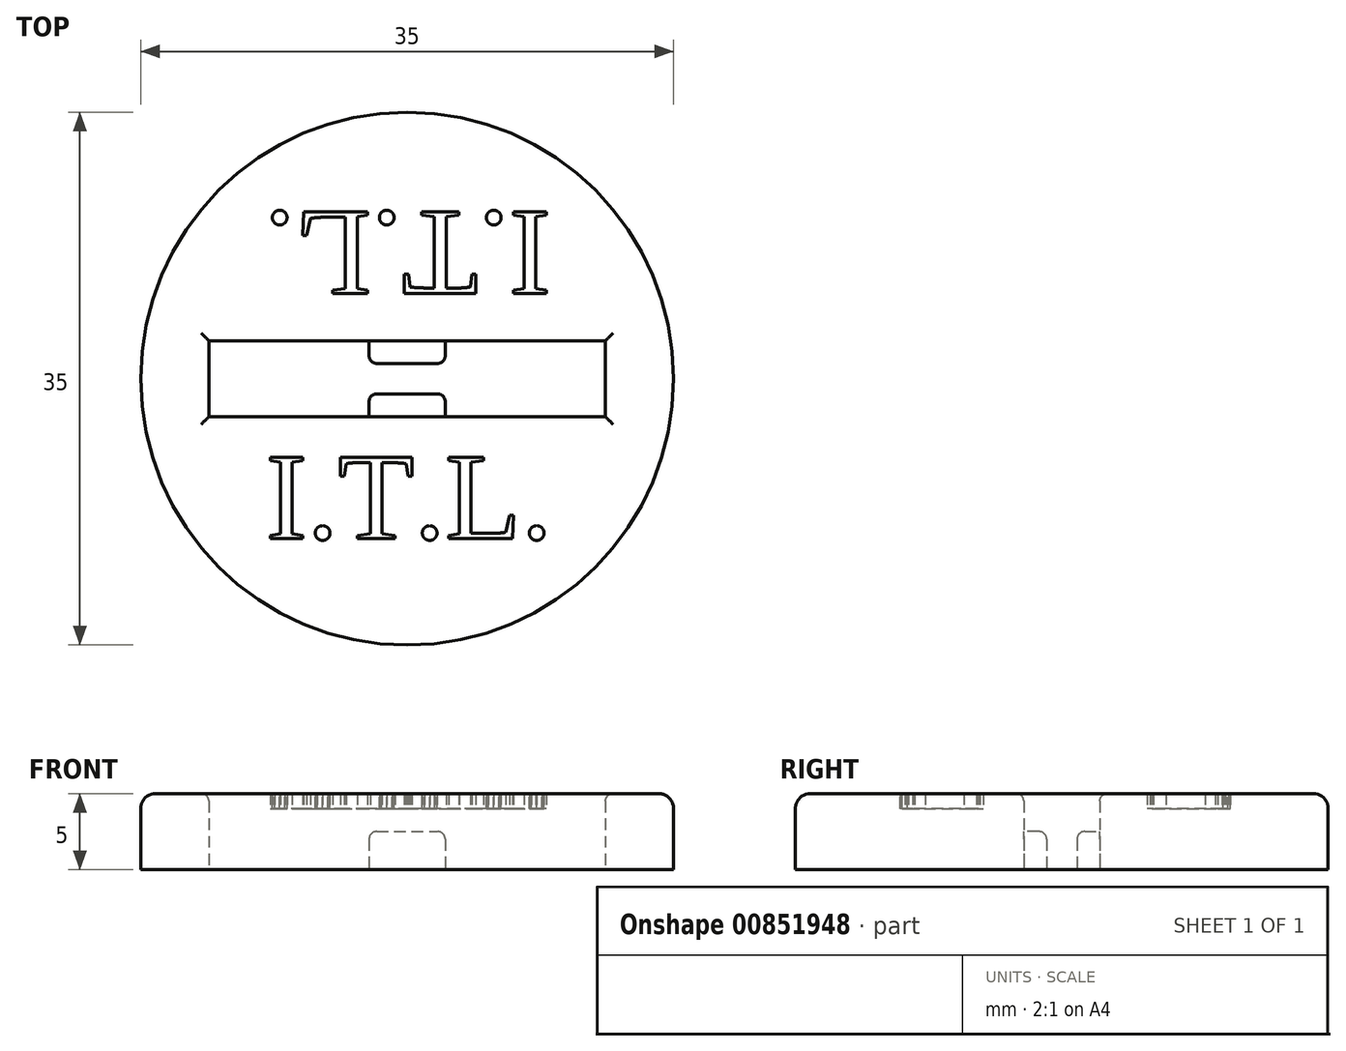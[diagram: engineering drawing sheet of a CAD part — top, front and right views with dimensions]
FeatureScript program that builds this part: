
annotation { "Feature Type Name" : "Feature", "Feature Type Description" : "" }
export const myFeature = defineFeature(function(context is Context, id is Id, definition is map)
    precondition{}
    {
        {
            var Q0;
            Q0=qCreatedBy(makeId("Top.planeOp"),FACE);
            var sketch = newSketch(context, id + "F0", { "sketchPlane" : qUnion([Q0])});
            skPoint(sketch, "E0.middle", {"position": v(0, 0) * mm});
            skLineSegment(sketch, "E1", {"start": v(2.5, -1) * mm, "end": v(-2.5, -1) * mm});
            skLineSegment(sketch, "E2", {"start": v(-2.5, 1) * mm, "end": v(2.5, 1) * mm});
            skCircle(sketch, "E3", {"center": v(0, 0) * mm, "radius": 17.5 * mm});
            skText(sketch, "E4", { "text": "I.T.L.", "fontName": "Tinos-Regular.ttf"});
            skText(sketch, "E5", { "text": "I.T.L.", "fontName": "Tinos-Regular.ttf"});
            skLineSegment(sketch, "E6", {"start": v(2.5, -1) * mm, "end": v(2.5, -2.5) * mm});
            skLineSegment(sketch, "E7", {"start": v(-2.5, -1) * mm, "end": v(-2.5, -2.5) * mm});
            skLineSegment(sketch, "E8", {"start": v(-2.5, 1) * mm, "end": v(-2.5, 2.5) * mm});
            skLineSegment(sketch, "E9", {"start": v(2.5, 1) * mm, "end": v(2.5, 2.5) * mm});
            skLineSegment(sketch, "E10", {"start": v(13.03, -2.5) * mm, "end": v(13.03, 2.5) * mm});
            skLineSegment(sketch, "E11", {"start": v(-13.03, 2.5) * mm, "end": v(-13.03, -2.5) * mm});
            skLineSegment(sketch, "E12", {"start": v(13.03, -2.5) * mm, "end": v(-13.03, -2.5) * mm});
            skLineSegment(sketch, "E13", {"start": v(-13.03, 2.5) * mm, "end": v(13.03, 2.5) * mm});
            const initialGuessF0  = {"E4": [-0.00929, -0.01051, 1, 0, 0.00588], "E5": [0.00943, 0.01095, -1, 0, 0.00588]};
            skSetInitialGuess(sketch, initialGuessF0);
            skSolve(sketch);
        }
        {
            var Q0;
            Q0 = qSketchRegion(id + "F0", true);
            extrude(context, id + "F1", {"entities" : qUnion([Q0]), "depth" : 5 * mm, "offsetDistance" : 25 * mm});
        }
        {
            var Q0;
            Q0=makeQuery(id+"F1.opExtrude","CAP_EDGE",EDGE,{"disambiguationData":[OSD([sQuery(id+"F0.wireOp",EDGE,"99ddf1c2-c051-48f3-a438-be00599b5eb5.bottom")])],"isStart":false});
            var Q1;
            Q1=makeQuery(id+"F1.opExtrude","CAP_EDGE",EDGE,{"disambiguationData":[OSD([sQuery(id+"F0.wireOp",EDGE,"99ddf1c2-c051-48f3-a438-be00599b5eb5.left")])],"isStart":false});
            var Q2;
            Q2=makeQuery(id+"F1.opExtrude","CAP_EDGE",EDGE,{"disambiguationData":[OSD([sQuery(id+"F0.wireOp",EDGE,"99ddf1c2-c051-48f3-a438-be00599b5eb5.top")])],"isStart":false});
            var Q3;
            Q3=makeQuery(id+"F1.opExtrude","CAP_EDGE",EDGE,{"disambiguationData":[OSD([sQuery(id+"F0.wireOp",EDGE,"99ddf1c2-c051-48f3-a438-be00599b5eb5.right")])],"isStart":false});
            var Q4;
            Q4=makeQuery(id+"F1.opExtrude","CAP_EDGE",EDGE,{"disambiguationData":[OSD([sQuery(id+"F0.wireOp",EDGE,"E13")])],"isStart":false});
            var Q5;
            Q5=makeQuery(id+"F1.opExtrude","CAP_EDGE",EDGE,{"disambiguationData":[OSD([sQuery(id+"F0.wireOp",EDGE,"E10")])],"isStart":false});
            var Q6;
            Q6=makeQuery(id+"F1.opExtrude","CAP_EDGE",EDGE,{"disambiguationData":[OSD([sQuery(id+"F0.wireOp",EDGE,"E12")])],"isStart":false});
            var Q7;
            Q7=makeQuery(id+"F1.opExtrude","CAP_EDGE",EDGE,{"disambiguationData":[OSD([sQuery(id+"F0.wireOp",EDGE,"E11")])],"isStart":false});
            fillet(context, id + "F2", {"entities" : qUnion([Q0, Q1, Q2, Q3, Q4, Q5, Q6, Q7]), "radius" : .5 * mm, "tangentPropagation" : true, "defaultsChanged" : false, "vertexSettings" : [], "allowEdgeOverflow" : false});
        }
        {
            var Q0;
            Q0=makeQuery(id+"F1.opExtrude","CAP_EDGE",EDGE,{"disambiguationData":[OSD([sQuery(id+"F0.wireOp",EDGE,"E3")])],"isStart":false});
            fillet(context, id + "F3", {"entities" : qUnion([Q0]), "radius" : 1 * mm, "tangentPropagation" : true, "allowEdgeOverflow" : false});
        }
        {
            var Q0;
            Q0=makeQuery(id+"F0.imprint","IMPRINT",FACE,{"disambiguationData":[TD([[makeQuery(id+"F0.imprint","IMPRINT",EDGE,{"derivedFrom":sQuery(id+"F0.wireOp",EDGE,"E2")}),1.0]])]});
            var Q1;
            Q1=makeQuery(id+"F0.imprint","IMPRINT",FACE,{"disambiguationData":[TD([[makeQuery(id+"F0.imprint","IMPRINT",EDGE,{"derivedFrom":sQuery(id+"F0.wireOp",EDGE,"E1")}),1.0]])]});
            extrude(context, id + "F4", {"entities" : qUnion([Q0, Q1]), "operationType" : NewBodyOperationType.ADD, "depth" : 2.5 * mm, "offsetDistance" : 25 * mm});
        }
        {
            var Q0;
            Q0=makeQuery(id+"F0.imprint","IMPRINT",FACE,{"disambiguationData":[TD([[makeQuery(id+"F0.imprint","IMPRINT",EDGE,{"derivedFrom":sQuery(id+"F0.wireOp",EDGE,"E4.sketch_text.stroke-47")}),-1.0]])]});
            var Q1;
            Q1=makeQuery(id+"F0.imprint","IMPRINT",FACE,{"disambiguationData":[TD([[makeQuery(id+"F0.imprint","IMPRINT",EDGE,{"derivedFrom":sQuery(id+"F0.wireOp",EDGE,"E4.sketch_text.stroke-62")}),-1.0]])]});
            var Q2;
            Q2=makeQuery(id+"F0.imprint","IMPRINT",FACE,{"disambiguationData":[TD([[makeQuery(id+"F0.imprint","IMPRINT",EDGE,{"derivedFrom":sQuery(id+"F0.wireOp",EDGE,"E4.sketch_text.stroke-39")}),-1.0]])]});
            var Q3;
            Q3=makeQuery(id+"F0.imprint","IMPRINT",FACE,{"disambiguationData":[TD([[makeQuery(id+"F0.imprint","IMPRINT",EDGE,{"derivedFrom":sQuery(id+"F0.wireOp",EDGE,"E4.sketch_text.stroke-20")}),-1.0]])]});
            var Q4;
            Q4=makeQuery(id+"F0.imprint","IMPRINT",FACE,{"disambiguationData":[TD([[makeQuery(id+"F0.imprint","IMPRINT",EDGE,{"derivedFrom":sQuery(id+"F0.wireOp",EDGE,"E4.sketch_text.stroke-12")}),-1.0]])]});
            var Q5;
            Q5=makeQuery(id+"F0.imprint","IMPRINT",FACE,{"disambiguationData":[TD([[makeQuery(id+"F0.imprint","IMPRINT",EDGE,{"derivedFrom":sQuery(id+"F0.wireOp",EDGE,"E4.sketch_text.stroke-0")}),-1.0]])]});
            extrude(context, id + "F5", {"entities" : qUnion([Q0, Q1, Q2, Q3, Q4, Q5]), "operationType" : NewBodyOperationType.ADD, "depth" : 4 * mm, "offsetDistance" : 25 * mm});
        }
        {
            var Q0;
            Q0=makeQuery(id+"F0.imprint","IMPRINT",FACE,{"disambiguationData":[TD([[makeQuery(id+"F0.imprint","IMPRINT",EDGE,{"derivedFrom":sQuery(id+"F0.wireOp",EDGE,"E5.sketch_text.stroke-0")}),-1.0]])]});
            var Q1;
            Q1=makeQuery(id+"F0.imprint","IMPRINT",FACE,{"disambiguationData":[TD([[makeQuery(id+"F0.imprint","IMPRINT",EDGE,{"derivedFrom":sQuery(id+"F0.wireOp",EDGE,"E5.sketch_text.stroke-12")}),-1.0]])]});
            var Q2;
            Q2=makeQuery(id+"F0.imprint","IMPRINT",FACE,{"disambiguationData":[TD([[makeQuery(id+"F0.imprint","IMPRINT",EDGE,{"derivedFrom":sQuery(id+"F0.wireOp",EDGE,"E5.sketch_text.stroke-20")}),-1.0]])]});
            var Q3;
            Q3=makeQuery(id+"F0.imprint","IMPRINT",FACE,{"disambiguationData":[TD([[makeQuery(id+"F0.imprint","IMPRINT",EDGE,{"derivedFrom":sQuery(id+"F0.wireOp",EDGE,"E5.sketch_text.stroke-39")}),-1.0]])]});
            var Q4;
            Q4=makeQuery(id+"F0.imprint","IMPRINT",FACE,{"disambiguationData":[TD([[makeQuery(id+"F0.imprint","IMPRINT",EDGE,{"derivedFrom":sQuery(id+"F0.wireOp",EDGE,"E5.sketch_text.stroke-47")}),-1.0]])]});
            var Q5;
            Q5=makeQuery(id+"F0.imprint","IMPRINT",FACE,{"disambiguationData":[TD([[makeQuery(id+"F0.imprint","IMPRINT",EDGE,{"derivedFrom":sQuery(id+"F0.wireOp",EDGE,"E5.sketch_text.stroke-62")}),-1.0]])]});
            extrude(context, id + "F6", {"entities" : qUnion([Q0, Q1, Q2, Q3, Q4, Q5]), "operationType" : NewBodyOperationType.ADD, "depth" : 4 * mm, "offsetDistance" : 25 * mm});
        }
        {
            var Q0;
            Q0=makeQuery(id+"F4.opExtrude","CAP_EDGE",EDGE,{"disambiguationData":[OSD([sQuery(id+"F0.wireOp",EDGE,"E8")])],"isStart":false});
            var Q1;
            Q1=makeQuery(id+"F4.opExtrude","CAP_EDGE",EDGE,{"disambiguationData":[OSD([sQuery(id+"F0.wireOp",EDGE,"E2")])],"isStart":false});
            var Q2;
            Q2=makeQuery(id+"F4.opExtrude","CAP_EDGE",EDGE,{"disambiguationData":[OSD([sQuery(id+"F0.wireOp",EDGE,"E9")])],"isStart":false});
            var Q3;
            Q3=makeQuery(id+"F4.opExtrude","CAP_EDGE",EDGE,{"disambiguationData":[OSD([sQuery(id+"F0.wireOp",EDGE,"E7")])],"isStart":false});
            var Q4;
            Q4=makeQuery(id+"F4.opExtrude","CAP_EDGE",EDGE,{"disambiguationData":[OSD([sQuery(id+"F0.wireOp",EDGE,"E1")])],"isStart":false});
            var Q5;
            Q5=makeQuery(id+"F4.opExtrude","CAP_EDGE",EDGE,{"disambiguationData":[OSD([sQuery(id+"F0.wireOp",EDGE,"E6")])],"isStart":false});
            var Q6;
            Q6=makeQuery(id+"F4.opExtrude","SWEPT_EDGE",EDGE,{"disambiguationData":[OSD([sQuery(id+"F0.wireOp",EDGE,"E1"),sQuery(id+"F0.wireOp",EDGE,"E6")])]});
            var Q7;
            Q7=makeQuery(id+"F4.opExtrude","SWEPT_EDGE",EDGE,{"disambiguationData":[OSD([sQuery(id+"F0.wireOp",EDGE,"E2"),sQuery(id+"F0.wireOp",EDGE,"E9")])]});
            var Q8;
            Q8=makeQuery(id+"F4.opExtrude","SWEPT_EDGE",EDGE,{"disambiguationData":[OSD([sQuery(id+"F0.wireOp",EDGE,"E2"),sQuery(id+"F0.wireOp",EDGE,"E8")])]});
            var Q9;
            Q9=makeQuery(id+"F4.opExtrude","SWEPT_EDGE",EDGE,{"disambiguationData":[OSD([sQuery(id+"F0.wireOp",EDGE,"E1"),sQuery(id+"F0.wireOp",EDGE,"E7")])]});
            fillet(context, id + "F7", {"entities" : qUnion([Q0, Q1, Q2, Q3, Q4, Q5, Q6, Q7, Q8, Q9]), "tangentPropagation" : true, "radius" : .5 * mm, "defaultsChanged" : false, "vertexSettings" : [], "allowEdgeOverflow" : false});
        }
    });
